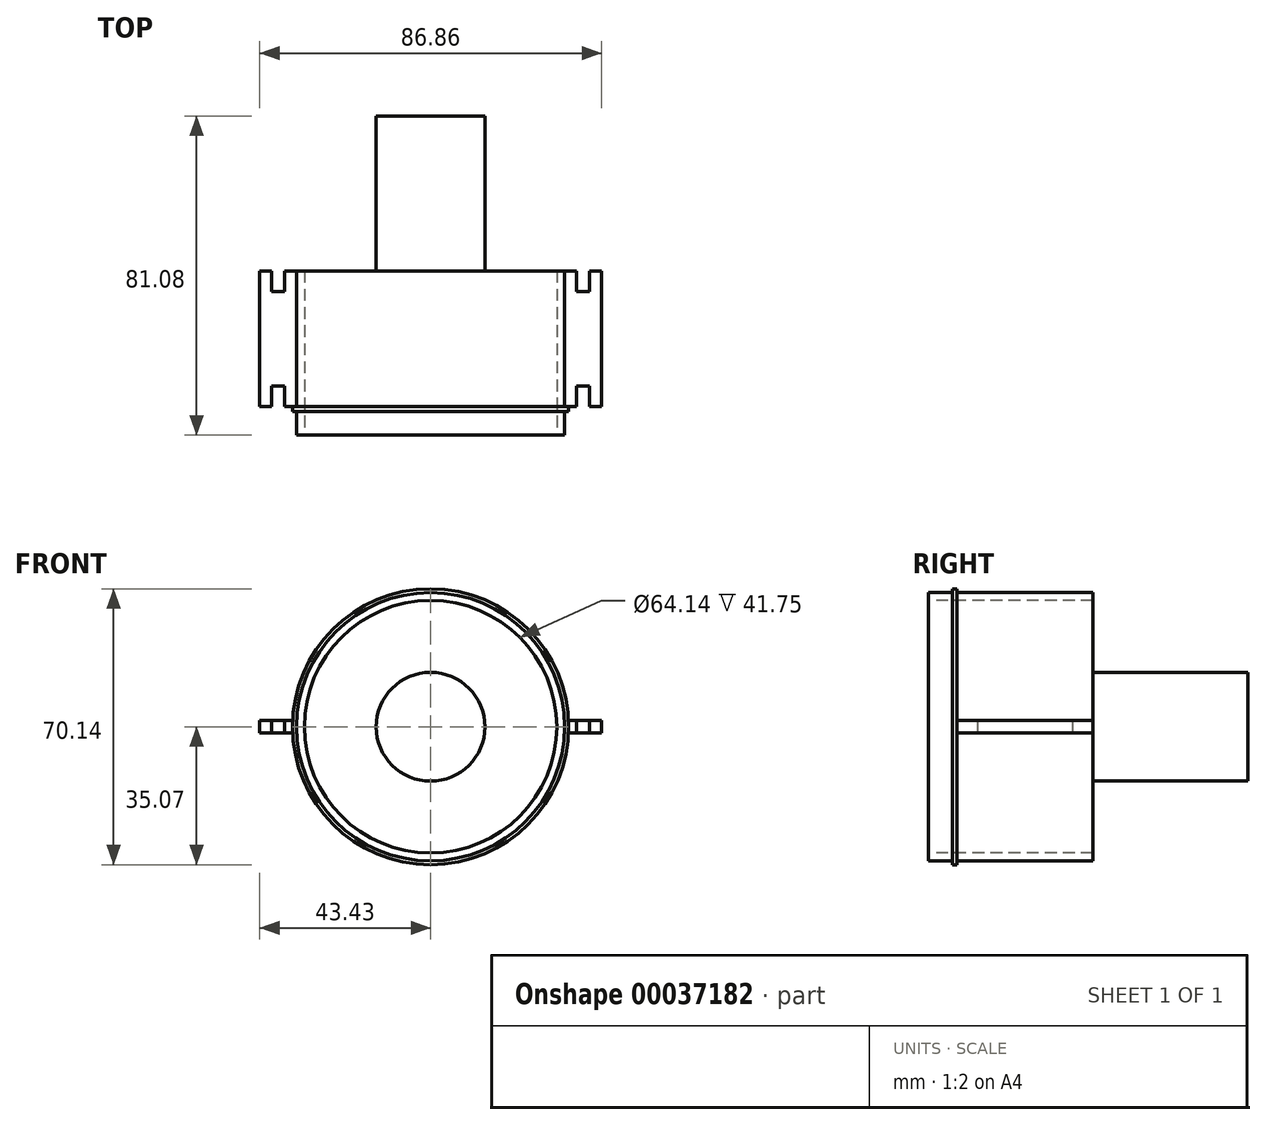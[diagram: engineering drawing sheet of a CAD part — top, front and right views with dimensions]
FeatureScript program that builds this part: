
annotation { "Feature Type Name" : "Feature", "Feature Type Description" : "" }
export const myFeature = defineFeature(function(context is Context, id is Id, definition is map)
    precondition{}
    {
        {
            var Q0;
            Q0=qCreatedBy(makeId("Front.planeOp"),FACE);
            var sketch = newSketch(context, id + "F0", { "sketchPlane" : qUnion([Q0])});
            skCircle(sketch, "E0", {"center": v(0, 0) * mm, "radius": 32.07 * mm});
            skCircle(sketch, "E1.0", {"center": v(0, 0) * mm, "radius": 34.07 * mm});
            skSolve(sketch);
        }
        {
            var Q0;
            Q0=qCreatedBy(makeId("Front.planeOp"),FACE);
            cPlane(context, id + "F1", {"entities" : qUnion([Q0]), "cplaneType" : CPlaneType.OFFSET, "offset" : 7.24 * mm, "oppositeDirection" : true, "width" : 150 * mm, "height" : 150 * mm});
        }
        {
            var Q0;
            Q0=qCreatedBy(id+"F1.planeOp",FACE);
            var sketch = newSketch(context, id + "F2", { "sketchPlane" : qUnion([Q0])});
            skCircle(sketch, "E2.0", {"center": v(0, 0) * mm, "radius": 32.07 * mm});
            skCircle(sketch, "E3.0", {"center": v(0, 0) * mm, "radius": 35.07 * mm});
            skSolve(sketch);
        }
        {
            var Q0;
            Q0 = qSketchRegion(id + "F0", true);
            var Q1;
            Q1=qCreatedBy(id+"F1.planeOp",FACE);
            extrude(context, id + "F3", {"entities" : qUnion([Q0]), "endBound" : BoundingType.UP_TO_SURFACE, "oppositeDirection" : true, "endBoundEntityFace" : qUnion([Q1]), "depth" : 25 * mm});
        }
        {
            var Q0;
            Q0 = qSketchRegion(id + "F2", true);
            extrude(context, id + "F4", {"entities" : qUnion([Q0]), "operationType" : NewBodyOperationType.ADD, "depth" : 1.2 * mm});
        }
        {
            var Q0;
            Q0=qCreatedBy(makeId("Front.planeOp"),FACE);
            cPlane(context, id + "F5", {"entities" : qUnion([Q0]), "cplaneType" : CPlaneType.OFFSET, "offset" : 7.24 * mm, "oppositeDirection" : true, "width" : 150 * mm, "height" : 150 * mm});
        }
        {
            var Q0;
            Q0=qCreatedBy(id+"F5.planeOp",FACE);
            var sketch = newSketch(context, id + "F6", { "sketchPlane" : qUnion([Q0])});
            skCircle(sketch, "E4.0", {"center": v(0, 0) * mm, "radius": 32.07 * mm});
            skCircle(sketch, "E4.1", {"center": v(0, 0) * mm, "radius": 34.07 * mm});
            skSolve(sketch);
        }
        {
            var Q0;
            Q0 = qSketchRegion(id + "F6", true);
            extrude(context, id + "F7", {"entities" : qUnion([Q0]), "operationType" : NewBodyOperationType.ADD, "oppositeDirection" : true, "depth" : 34.5 * mm});
        }
        {
            var Q0;
            Q0=qCreatedBy(makeId("Front.planeOp"),FACE);
            cPlane(context, id + "F8", {"entities" : qUnion([Q0]), "cplaneType" : CPlaneType.OFFSET, "offset" : 41.75 * mm, "oppositeDirection" : true, "width" : 150 * mm, "height" : 150 * mm});
        }
        {
            var Q0;
            Q0=qCreatedBy(id+"F8.planeOp",FACE);
            var sketch = newSketch(context, id + "F9", { "sketchPlane" : qUnion([Q0])});
            skCircle(sketch, "E5", {"center": v(0, 0) * mm, "radius": 13.81 * mm});
            skSolve(sketch);
        }
        {
            var Q0;
            Q0 = qSketchRegion(id + "F9", true);
            extrude(context, id + "F10", {"entities" : qUnion([Q0]), "oppositeDirection" : true, "depth" : 39.33 * mm});
        }
        {
            var Q0;
            Q0=qCreatedBy(makeId("Top.planeOp"),FACE);
            var sketch = newSketch(context, id + "F11", { "sketchPlane" : qUnion([Q0])});
            skLineSegment(sketch, "E6", {"start": v(-34.07, 41.75) * mm, "end": v(-34.07, 7.24) * mm});
            skLineSegment(sketch, "E7", {"start": v(35.07, 7.24) * mm, "end": v(35.07, 6.04) * mm});
            skLineSegment(sketch, "E8.MirrorCS", {"start": v(-43.43, 7.24) * mm, "end": v(-43.43, 41.75) * mm});
            skLineSegment(sketch, "E9", {"start": v(-43.43, 41.75) * mm, "end": v(-40.43, 41.75) * mm});
            skLineSegment(sketch, "E10", {"start": v(-43.43, 7.24) * mm, "end": v(-40.43, 7.24) * mm});
            skLineSegment(sketch, "E11", {"start": v(34.07, 7.24) * mm, "end": v(37.07, 7.24) * mm});
            skLineSegment(sketch, "E12", {"start": v(34.07, 41.75) * mm, "end": v(37.07, 41.75) * mm});
            skLineSegment(sketch, "E13.0", {"start": v(-40.43, 36.54) * mm, "end": v(-37.07, 36.54) * mm});
            skLineSegment(sketch, "E14.0", {"start": v(-40.43, 12.45) * mm, "end": v(-37.07, 12.45) * mm});
            skLineSegment(sketch, "E15.0", {"start": v(37.07, 12.45) * mm, "end": v(40.43, 12.45) * mm});
            skLineSegment(sketch, "E16.0", {"start": v(37.07, 36.54) * mm, "end": v(40.43, 36.54) * mm});
            skLineSegment(sketch, "E17.0", {"start": v(40.43, 7.24) * mm, "end": v(40.43, 12.45) * mm});
            skLineSegment(sketch, "E18.0", {"start": v(37.07, 7.24) * mm, "end": v(37.07, 12.45) * mm});
            skLineSegment(sketch, "E19.MirrorCS", {"start": v(-37.07, 7.24) * mm, "end": v(-37.07, 12.45) * mm});
            skLineSegment(sketch, "E20.MirrorCS", {"start": v(-40.43, 7.24) * mm, "end": v(-40.43, 12.45) * mm});
            skLineSegment(sketch, "E21.trimOffspring", {"start": v(-37.07, 41.75) * mm, "end": v(-34.07, 41.75) * mm});
            skLineSegment(sketch, "E22.trimOffspring", {"start": v(-37.07, 7.24) * mm, "end": v(-34.07, 7.24) * mm});
            skLineSegment(sketch, "E23.trimOffspring", {"start": v(40.43, 41.75) * mm, "end": v(43.43, 41.75) * mm});
            skLineSegment(sketch, "E24.trimOffspring", {"start": v(40.43, 7.24) * mm, "end": v(43.43, 7.24) * mm});
            skLineSegment(sketch, "E25.trimOffspring", {"start": v(-40.43, 36.54) * mm, "end": v(-40.43, 41.75) * mm});
            skLineSegment(sketch, "E26.trimOffspring", {"start": v(-37.07, 36.54) * mm, "end": v(-37.07, 41.75) * mm});
            skLineSegment(sketch, "E27.trimOffspring", {"start": v(37.07, 36.54) * mm, "end": v(37.07, 41.75) * mm});
            skLineSegment(sketch, "E28.trimOffspring", {"start": v(40.43, 36.54) * mm, "end": v(40.43, 41.75) * mm});
            skPoint(sketch, "E29.end.orphan", {"position": v(34.07, 41.75) * mm});
            skPoint(sketch, "E29.start.orphan", {"position": v(34.07, 7.24) * mm});
            skLineSegment(sketch, "E30", {"start": v(34.07, 7.24) * mm, "end": v(34.07, 41.75) * mm});
            skLineSegment(sketch, "E31", {"start": v(43.43, 7.24) * mm, "end": v(43.43, 41.75) * mm});
            skLineSegment(sketch, "E32", {"start": v(-34.07, 7.24) * mm, "end": v(-34.07, 41.75) * mm});
            skSolve(sketch);
        }
        {
            var Q0;
            Q0 = qSketchRegion(id + "F11", true);
            extrude(context, id + "F12", {"entities" : qUnion([Q0]), "depth" : 3.2 * mm, "symmetric" : true});
        }
    });
